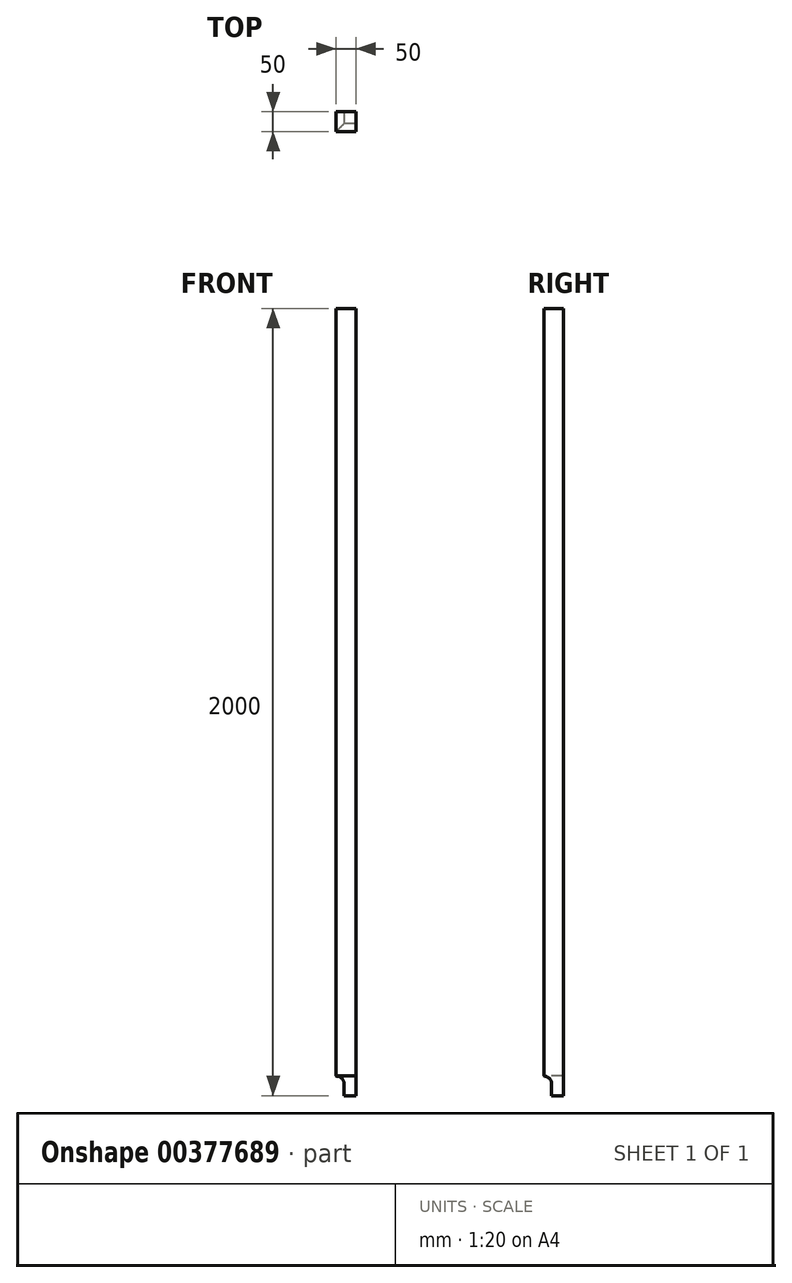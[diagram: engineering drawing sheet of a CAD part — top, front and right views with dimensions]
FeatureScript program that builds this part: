
annotation { "Feature Type Name" : "Feature", "Feature Type Description" : "" }
export const myFeature = defineFeature(function(context is Context, id is Id, definition is map)
    precondition{}
    {
        {
            var Q0;
            Q0=qCreatedBy(makeId("Top.planeOp"),FACE);
            var sketch = newSketch(context, id + "F0", { "sketchPlane" : qUnion([Q0])});
            skLineSegment(sketch, "E0.bottom", {"start": v(0, 0) * mm, "end": v(50, 0) * mm});
            skLineSegment(sketch, "E0.top", {"start": v(0, 50) * mm, "end": v(50, 50) * mm});
            skLineSegment(sketch, "E0.left", {"start": v(0, 0) * mm, "end": v(0, 50) * mm});
            skLineSegment(sketch, "E0.right", {"start": v(50, 0) * mm, "end": v(50, 50) * mm});
            skSolve(sketch);
        }
        {
            var Q0;
            Q0=makeQuery(id+"F0.imprint","IMPRINT",FACE,{"disambiguationData":[TD([[makeQuery(id+"F0.imprint","IMPRINT",EDGE,{"derivedFrom":sQuery(id+"F0.wireOp",EDGE,"E0.bottom")}),1.0]])]});
            extrude(context, id + "F1", {"entities" : qUnion([Q0]), "depth" : 2000 * mm});
        }
        {
            var Q0;
            Q0=qCreatedBy(makeId("Front.planeOp"),FACE);
            var sketch = newSketch(context, id + "F2", { "sketchPlane" : qUnion([Q0])});
            skLineSegment(sketch, "E1.bottom", {"start": v(0, 0) * mm, "end": v(20, 0) * mm});
            skLineSegment(sketch, "E1.top", {"start": v(0, 50) * mm, "end": v(0, 50) * mm});
            skLineSegment(sketch, "E1.left", {"start": v(0, 0) * mm, "end": v(0, 50) * mm});
            skLineSegment(sketch, "E1.right", {"start": v(20, 0) * mm, "end": v(20, 30) * mm});
            skPoint(sketch, "E2.visualSharp", {"position": v(20, 50) * mm});
            skArc(sketch, "E2.filletArc", {"start": v(20, 30) * mm, "mid": v(14.14, 44.14) * mm, "end": v(0, 50) * mm});
            skSolve(sketch);
        }
        {
            var Q0;
            Q0=makeQuery(id+"F2.imprint","IMPRINT",FACE,{"disambiguationData":[TD([[makeQuery(id+"F2.imprint","IMPRINT",EDGE,{"derivedFrom":sQuery(id+"F2.wireOp",EDGE,"E1.bottom")}),1.0]])]});
            extrude(context, id + "F3", {"entities" : qUnion([Q0]), "operationType" : NewBodyOperationType.REMOVE, "endBound" : BoundingType.THROUGH_ALL, "oppositeDirection" : true, "depth" : 25 * mm});
        }
        {
            var Q0;
            Q0=qCreatedBy(makeId("Right.planeOp"),FACE);
            var sketch = newSketch(context, id + "F4", { "sketchPlane" : qUnion([Q0])});
            skLineSegment(sketch, "E3.bottom", {"start": v(0, 0) * mm, "end": v(20, 0) * mm});
            skLineSegment(sketch, "E3.top", {"start": v(0, 50) * mm, "end": v(0, 50) * mm});
            skLineSegment(sketch, "E3.left", {"start": v(0, 0) * mm, "end": v(0, 50) * mm});
            skLineSegment(sketch, "E3.right", {"start": v(20, 0) * mm, "end": v(20, 30) * mm});
            skPoint(sketch, "E4.visualSharp", {"position": v(20, 50) * mm});
            skArc(sketch, "E4.filletArc", {"start": v(20, 30) * mm, "mid": v(14.14, 44.14) * mm, "end": v(0, 50) * mm});
            skSolve(sketch);
        }
        {
            var Q0;
            Q0=makeQuery(id+"F4.imprint","IMPRINT",FACE,{"disambiguationData":[TD([[makeQuery(id+"F4.imprint","IMPRINT",EDGE,{"derivedFrom":sQuery(id+"F4.wireOp",EDGE,"E3.bottom")}),1.0]])]});
            extrude(context, id + "F5", {"entities" : qUnion([Q0]), "operationType" : NewBodyOperationType.REMOVE, "endBound" : BoundingType.THROUGH_ALL, "depth" : 25 * mm});
        }
    });
